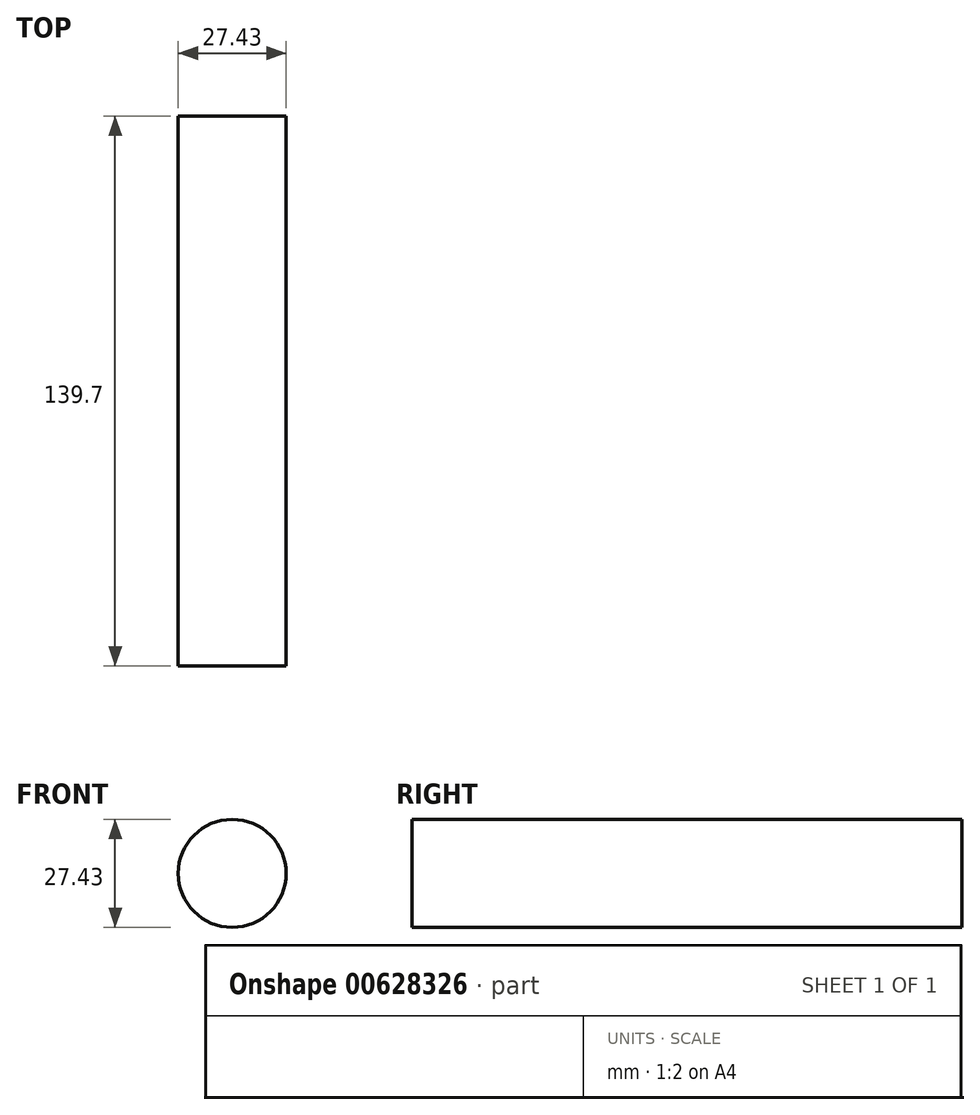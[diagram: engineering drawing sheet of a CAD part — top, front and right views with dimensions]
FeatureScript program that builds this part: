
annotation { "Feature Type Name" : "Feature", "Feature Type Description" : "" }
export const myFeature = defineFeature(function(context is Context, id is Id, definition is map)
    precondition{}
    {
        {
            var Q0;
            Q0=qCreatedBy(makeId("Front.planeOp"),FACE);
            var sketch = newSketch(context, id + "F0", { "sketchPlane" : qUnion([Q0])});
            skCircle(sketch, "E0", {"center": v(-4.32, 10.04) * mm, "radius": 13.72 * mm});
            skSolve(sketch);
        }
        {
            var Q0;
            Q0=makeQuery(id+"F0.imprint","IMPRINT",FACE,{"disambiguationData":[TD([[makeQuery(id+"F0.imprint","IMPRINT",EDGE,{"derivedFrom":sQuery(id+"F0.wireOp",EDGE,"E0")}),1.0]])]});
            extrude(context, id + "F1", {"entities" : qUnion([Q0]), "depth" : 139.7 * mm, "offsetDistance" : 25.4 * mm});
        }
    });
